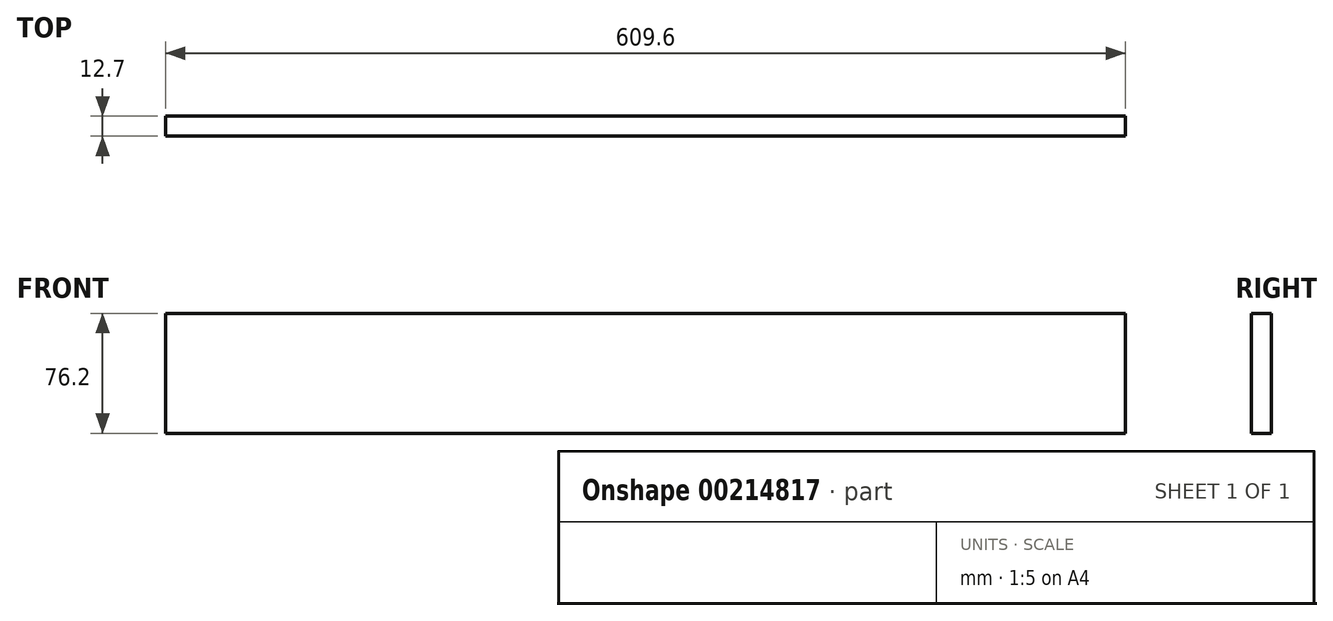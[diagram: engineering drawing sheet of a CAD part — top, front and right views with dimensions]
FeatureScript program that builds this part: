
annotation { "Feature Type Name" : "Feature", "Feature Type Description" : "" }
export const myFeature = defineFeature(function(context is Context, id is Id, definition is map)
    precondition{}
    {
        {
            var Q0;
            Q0=qCreatedBy(makeId("Front.planeOp"),FACE);
            var sketch = newSketch(context, id + "F0", { "sketchPlane" : qUnion([Q0])});
            skLineSegment(sketch, "E0.bottom", {"start": v(0, 0) * mm, "end": v(609.6, 0) * mm});
            skLineSegment(sketch, "E0.top", {"start": v(0, -76.2) * mm, "end": v(609.6, -76.2) * mm});
            skLineSegment(sketch, "E0.left", {"start": v(0, 0) * mm, "end": v(0, -76.2) * mm});
            skLineSegment(sketch, "E0.right", {"start": v(609.6, 0) * mm, "end": v(609.6, -76.2) * mm});
            skSolve(sketch);
        }
        {
            var Q0;
            Q0=makeQuery(id+"F0.imprint","IMPRINT",FACE,{"disambiguationData":[TD([[makeQuery(id+"F0.imprint","IMPRINT",EDGE,{"derivedFrom":sQuery(id+"F0.wireOp",EDGE,"E0.bottom")}),-1.0]])]});
            extrude(context, id + "F1", {"entities" : qUnion([Q0]), "depth" : 12.7 * mm});
        }
    });
